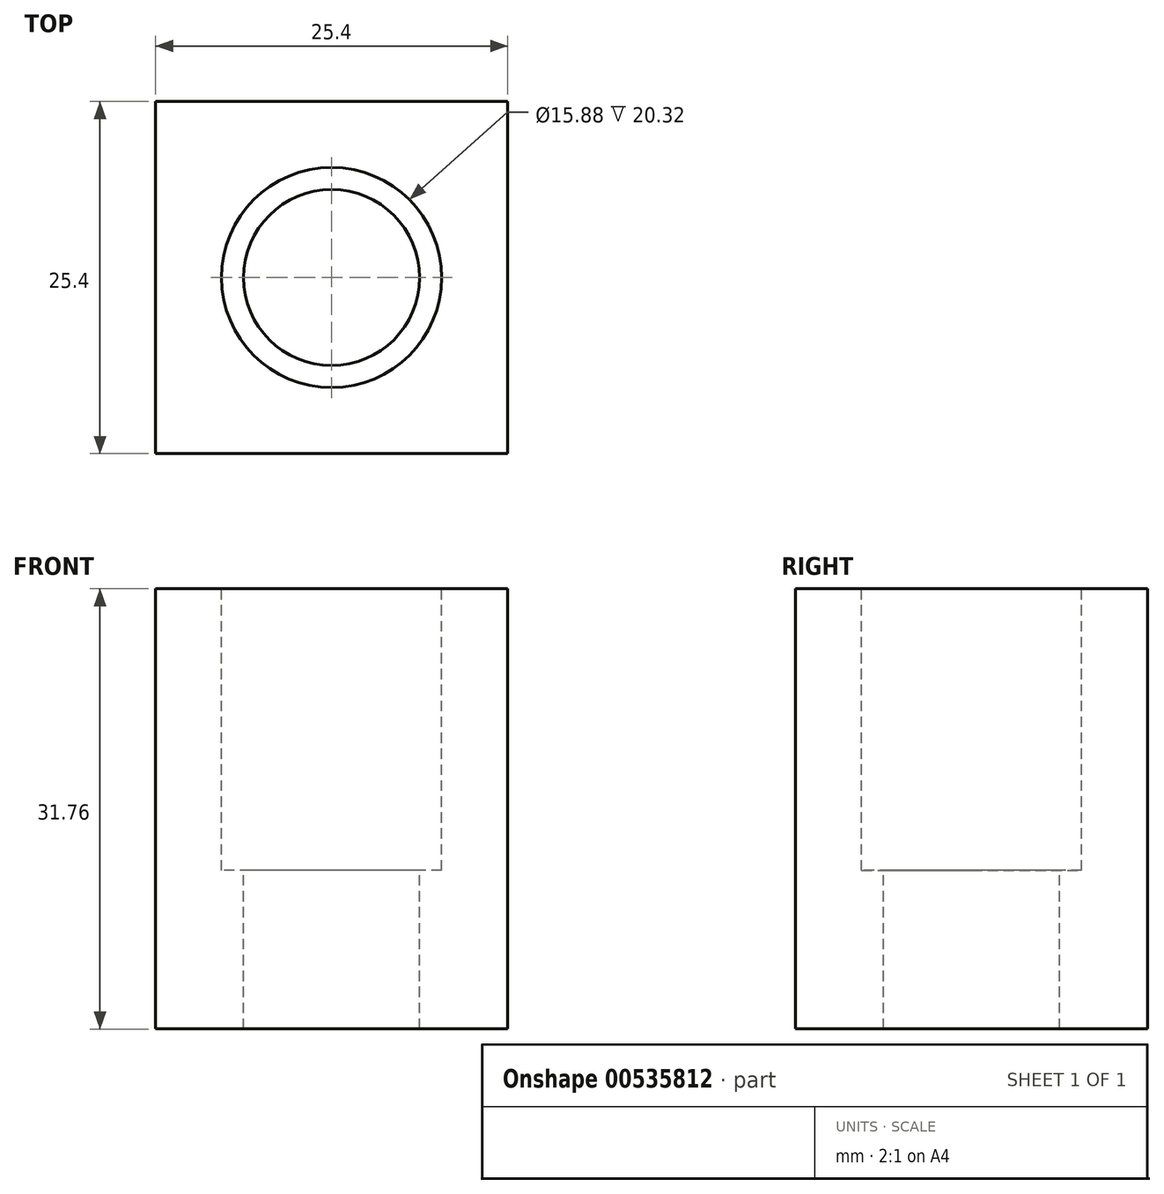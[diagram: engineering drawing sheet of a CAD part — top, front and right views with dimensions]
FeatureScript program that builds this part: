
annotation { "Feature Type Name" : "Feature", "Feature Type Description" : "" }
export const myFeature = defineFeature(function(context is Context, id is Id, definition is map)
    precondition{}
    {
        {
            var Q0;
            Q0=qCreatedBy(makeId("Front.planeOp"),FACE);
            var sketch = newSketch(context, id + "F0", { "sketchPlane" : qUnion([Q0])});
            skLineSegment(sketch, "E0.bottom", {"start": v(12.7, 15.88) * mm, "end": v(-12.7, 15.88) * mm});
            skLineSegment(sketch, "E0.top", {"start": v(12.7, -15.88) * mm, "end": v(-12.7, -15.88) * mm});
            skLineSegment(sketch, "E0.left", {"start": v(12.7, 15.88) * mm, "end": v(12.7, -15.87) * mm});
            skLineSegment(sketch, "E0.right", {"start": v(-12.7, 15.88) * mm, "end": v(-12.7, -15.87) * mm});
            skPoint(sketch, "E0.middle", {"position": v(0, 0) * mm});
            skSolve(sketch);
        }
        {
            var Q0;
            Q0 = qSketchRegion(id + "F0", true);
            extrude(context, id + "F1", {"entities" : qUnion([Q0]), "depth" : 25.4 * mm, "offsetDistance" : 25.4 * mm});
        }
        {
            var Q0;
            Q0=makeQuery(id+"F1.opExtrude","SWEPT_FACE",FACE,{"disambiguationData":[OSD([sQuery(id+"F0.wireOp",EDGE,"E0.bottom")])]});
            var sketch = newSketch(context, id + "F2", { "sketchPlane" : qUnion([Q0])});
            skCircle(sketch, "E1", {"center": v(0, -12.7) * mm, "radius": 3.06 * mm});
            skPoint(sketch, "E1.centerSnap0", {"position": v(-12.7, -12.7) * mm});
            skPoint(sketch, "E1.centerSnap1", {"position": v(0, -25.4) * mm});
            skSolve(sketch);
        }
        {
            var Q0;
            Q0=sQuery(id+"F2.wireOp",VERTEX,"E1.center");
            var Q1;
            Q1=makeQuery(id+"F1.opExtrude","SWEPT_BODY",BODY,{"disambiguationData":[OSD([sQuery(id+"F0.wireOp",EDGE,"E0.bottom"),sQuery(id+"F0.wireOp",EDGE,"E0.top"),sQuery(id+"F0.wireOp",EDGE,"E0.left"),sQuery(id+"F0.wireOp",EDGE,"E0.right")])]});
            hole(context, id + "F3", {"style" : HoleStyle.C_BORE, "endStyle" : HoleEndStyle.THROUGH, "holeDiameter" : 12.7 * mm, "cBoreDiameter" : 15.88 * mm, "cBoreDepth" : 20.32 * mm, "isTappedThrough" : true, "tappedDepth" : 12.7 * mm, "tapClearance" : 3, "startFromSketch" : true, "locations" : qUnion([Q0]), "scope" : qUnion([Q1])});
        }
    });
